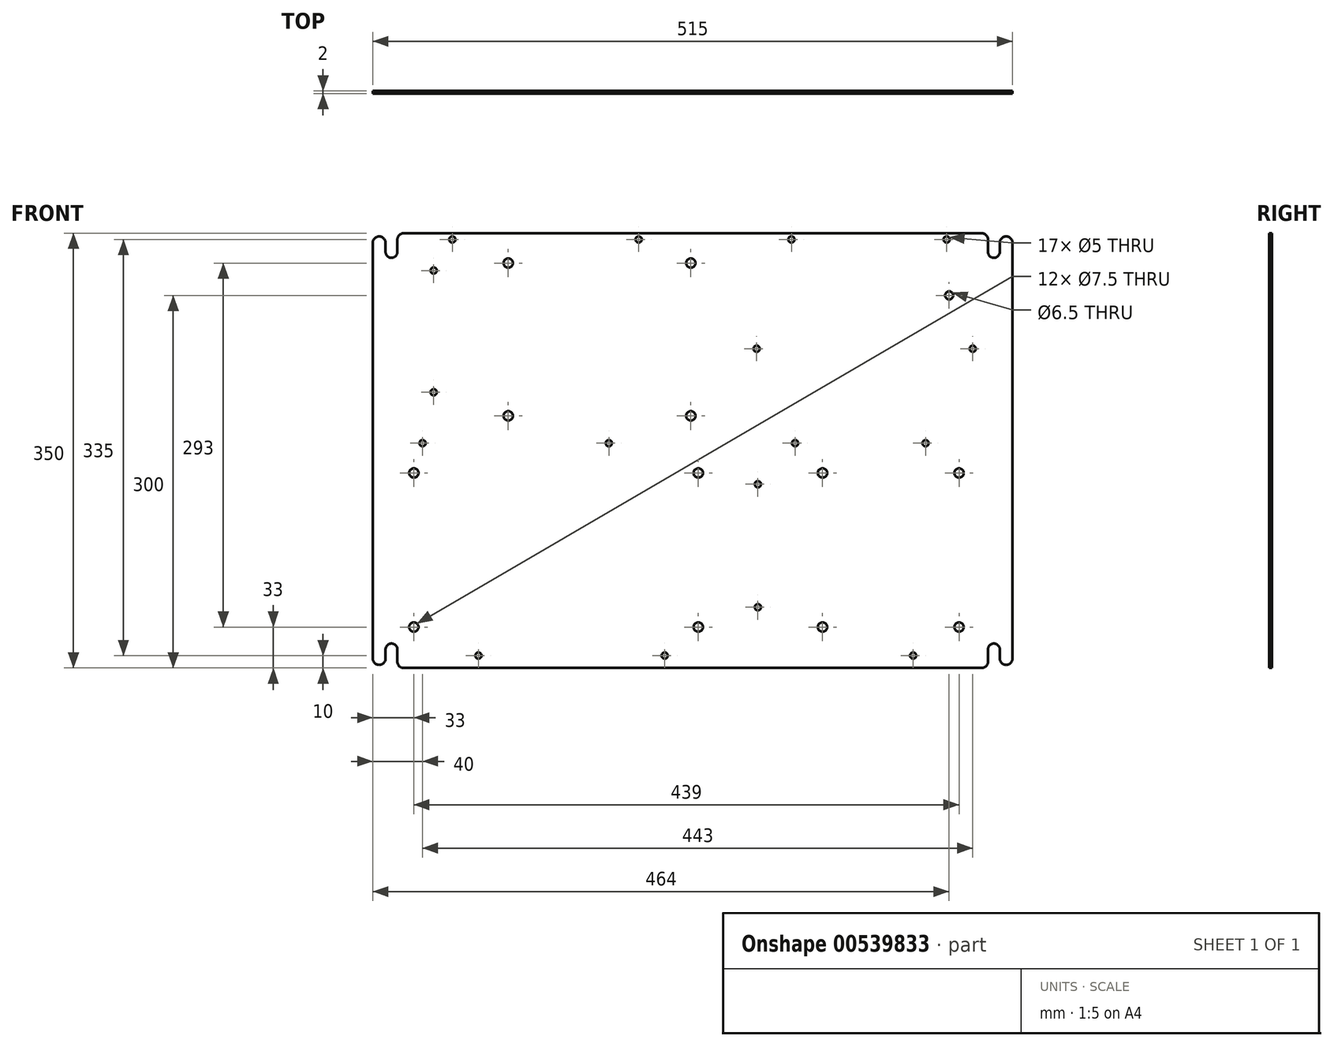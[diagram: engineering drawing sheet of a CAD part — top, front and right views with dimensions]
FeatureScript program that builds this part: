
annotation { "Feature Type Name" : "Feature", "Feature Type Description" : "" }
export const myFeature = defineFeature(function(context is Context, id is Id, definition is map)
    precondition{}
    {
        {
            var Q0;
            Q0=qCreatedBy(makeId("Front.planeOp"),FACE);
            var sketch = newSketch(context, id + "F0", { "sketchPlane" : qUnion([Q0])});
            skLineSegment(sketch, "E0.bottom", {"start": v(-257.5, -175) * mm, "end": v(232.75, -175) * mm});
            skLineSegment(sketch, "E0.top", {"start": v(-232.75, 175) * mm, "end": v(232.75, 175) * mm});
            skLineSegment(sketch, "E0.left", {"start": v(-257.5, -167.5) * mm, "end": v(-257.5, 167.5) * mm});
            skLineSegment(sketch, "E0.right", {"start": v(257.5, -167.5) * mm, "end": v(257.5, 167.5) * mm});
            skPoint(sketch, "E0.middle", {"position": v(0, 0) * mm});
            skArc(sketch, "E1", {"start": v(-247.25, 160) * mm, "mid": v(-242.5, 155.25) * mm, "end": v(-237.75, 160) * mm});
            skLineSegment(sketch, "E2", {"start": v(-247.25, 160) * mm, "end": v(-247.25, 167.5) * mm});
            skLineSegment(sketch, "E3", {"start": v(-237.75, 160) * mm, "end": v(-237.75, 170) * mm});
            skPoint(sketch, "E4.newPointB", {"position": v(-257.5, 175) * mm});
            skArc(sketch, "E4.filletArc", {"start": v(-232.75, 175) * mm, "mid": v(-236.29, 173.54) * mm, "end": v(-237.75, 170) * mm});
            skArc(sketch, "E5", {"start": v(-247.25, 167.5) * mm, "mid": v(-252.38, 172.48) * mm, "end": v(-257.5, 167.5) * mm});
            skPoint(sketch, "E5.endSnap0", {"position": v(-247.25, 167.5) * mm});
            skPoint(sketch, "E6.orphan", {"position": v(-247.25, 175) * mm});
            skArc(sketch, "E7.MirrorCS", {"start": v(247.25, 167.5) * mm, "mid": v(252.38, 172.48) * mm, "end": v(257.5, 167.5) * mm});
            skArc(sketch, "E8.MirrorCS", {"start": v(247.25, 160) * mm, "mid": v(242.5, 155.25) * mm, "end": v(237.75, 160) * mm});
            skLineSegment(sketch, "E9.MirrorCS", {"start": v(247.25, 160) * mm, "end": v(247.25, 167.5) * mm});
            skLineSegment(sketch, "E10.MirrorCS", {"start": v(237.75, 160) * mm, "end": v(237.75, 170) * mm});
            skArc(sketch, "E11.MirrorCS", {"start": v(232.75, 175) * mm, "mid": v(236.29, 173.54) * mm, "end": v(237.75, 170) * mm});
            skPoint(sketch, "E12.MirrorP", {"position": v(247.25, 175) * mm});
            skLineSegment(sketch, "E13.MirrorCS", {"start": v(232.75, 175) * mm, "end": v(-232.75, 175) * mm});
            skPoint(sketch, "E14.MirrorP", {"position": v(247.25, 167.5) * mm});
            skPoint(sketch, "E15.MirrorP", {"position": v(257.5, 175) * mm});
            skLineSegment(sketch, "E16.MirrorCS", {"start": v(232.75, -175) * mm, "end": v(-232.75, -175) * mm});
            skPoint(sketch, "E17.MirrorP", {"position": v(257.5, -175) * mm});
            skLineSegment(sketch, "E18.MirrorCS", {"start": v(257.5, 175) * mm, "end": v(257.5, -167.5) * mm});
            skLineSegment(sketch, "E19.MirrorCS", {"start": v(-232.75, -175) * mm, "end": v(232.75, -175) * mm});
            skLineSegment(sketch, "E20.MirrorCS", {"start": v(247.25, -160) * mm, "end": v(247.25, -167.5) * mm});
            skLineSegment(sketch, "E21.MirrorCS", {"start": v(237.75, -160) * mm, "end": v(237.75, -170) * mm});
            skArc(sketch, "E22.MirrorCS", {"start": v(247.25, -160) * mm, "mid": v(242.5, -155.25) * mm, "end": v(237.75, -160) * mm});
            skArc(sketch, "E23.MirrorCS", {"start": v(232.75, -175) * mm, "mid": v(236.29, -173.54) * mm, "end": v(237.75, -170) * mm});
            skPoint(sketch, "E24.MirrorP", {"position": v(247.25, -167.5) * mm});
            skPoint(sketch, "E25.MirrorP", {"position": v(247.25, -175) * mm});
            skArc(sketch, "E26.MirrorCS", {"start": v(247.25, -167.5) * mm, "mid": v(252.38, -172.48) * mm, "end": v(257.5, -167.5) * mm});
            skLineSegment(sketch, "E27.MirrorCS", {"start": v(-247.25, -160) * mm, "end": v(-247.25, -167.5) * mm});
            skArc(sketch, "E28.MirrorCS", {"start": v(-232.75, -175) * mm, "mid": v(-236.29, -173.54) * mm, "end": v(-237.75, -170) * mm});
            skArc(sketch, "E29.MirrorCS", {"start": v(-247.25, -167.5) * mm, "mid": v(-252.38, -172.48) * mm, "end": v(-257.5, -167.5) * mm});
            skArc(sketch, "E30.MirrorCS", {"start": v(-247.25, -160) * mm, "mid": v(-242.5, -155.25) * mm, "end": v(-237.75, -160) * mm});
            skLineSegment(sketch, "E31.MirrorCS", {"start": v(-237.75, -160) * mm, "end": v(-237.75, -170) * mm});
            skPoint(sketch, "E32.MirrorP", {"position": v(-247.25, -175) * mm});
            skLineSegment(sketch, "E33.MirrorCS", {"start": v(-257.5, 167.5) * mm, "end": v(-257.5, -167.5) * mm});
            skPoint(sketch, "E34.MirrorP", {"position": v(-247.25, -167.5) * mm});
            skPoint(sketch, "E35.MirrorP", {"position": v(-257.5, -175) * mm});
            skSolve(sketch);
        }
        {
            var Q0;
            Q0 = qSketchRegion(id + "F0", true);
            extrude(context, id + "F1", {"entities" : qUnion([Q0]), "depth" : 2 * mm, "offsetDistance" : 25 * mm});
        }
        {
            var Q0;
            Q0=makeQuery(id+"F1.opExtrude","CAP_FACE",FACE,{"disambiguationData":[OSD([sQuery(id+"F0.wireOp",EDGE,"E1"),sQuery(id+"F0.wireOp",EDGE,"E2"),sQuery(id+"F0.wireOp",EDGE,"E3"),sQuery(id+"F0.wireOp",EDGE,"E4.filletArc"),sQuery(id+"F0.wireOp",EDGE,"E5"),sQuery(id+"F0.wireOp",EDGE,"E7.MirrorCS"),sQuery(id+"F0.wireOp",EDGE,"E8.MirrorCS"),sQuery(id+"F0.wireOp",EDGE,"E9.MirrorCS"),sQuery(id+"F0.wireOp",EDGE,"E10.MirrorCS"),sQuery(id+"F0.wireOp",EDGE,"E11.MirrorCS"),sQuery(id+"F0.wireOp",EDGE,"E13.MirrorCS"),sQuery(id+"F0.wireOp",EDGE,"E20.MirrorCS"),sQuery(id+"F0.wireOp",EDGE,"E18.MirrorCS"),sQuery(id+"F0.wireOp",EDGE,"E21.MirrorCS"),sQuery(id+"F0.wireOp",EDGE,"E22.MirrorCS"),sQuery(id+"F0.wireOp",EDGE,"E23.MirrorCS"),sQuery(id+"F0.wireOp",EDGE,"E26.MirrorCS"),sQuery(id+"F0.wireOp",EDGE,"E27.MirrorCS"),sQuery(id+"F0.wireOp",EDGE,"E28.MirrorCS"),sQuery(id+"F0.wireOp",EDGE,"E29.MirrorCS"),sQuery(id+"F0.wireOp",EDGE,"E30.MirrorCS"),sQuery(id+"F0.wireOp",EDGE,"E31.MirrorCS"),sQuery(id+"F0.wireOp",EDGE,"E33.MirrorCS"),sQuery(id+"F0.wireOp",EDGE,"E19.MirrorCS")])],"isStart":false});
            var sketch = newSketch(context, id + "F2", { "sketchPlane" : qUnion([Q0])});
            skCircle(sketch, "E36", {"center": v(-172.5, -165) * mm, "radius": 2.5 * mm});
            skCircle(sketch, "E37", {"center": v(-22.5, -165) * mm, "radius": 2.5 * mm});
            skCircle(sketch, "E38", {"center": v(177.5, -165) * mm, "radius": 2.5 * mm});
            skCircle(sketch, "E39", {"center": v(-224.5, -142) * mm, "radius": 3.75 * mm});
            skCircle(sketch, "E40", {"center": v(-224.5, -18) * mm, "radius": 3.75 * mm});
            skCircle(sketch, "E41", {"center": v(4.5, -18) * mm, "radius": 3.75 * mm});
            skCircle(sketch, "E42", {"center": v(4.5, -142) * mm, "radius": 3.75 * mm});
            skCircle(sketch, "E43", {"center": v(52.5, -126) * mm, "radius": 2.5 * mm});
            skCircle(sketch, "E44", {"center": v(52.5, -27) * mm, "radius": 2.5 * mm});
            skCircle(sketch, "E45", {"center": v(104.5, -18) * mm, "radius": 3.75 * mm});
            skCircle(sketch, "E46", {"center": v(214.5, -18) * mm, "radius": 3.75 * mm});
            skCircle(sketch, "E47", {"center": v(104.5, -142) * mm, "radius": 3.75 * mm});
            skCircle(sketch, "E48", {"center": v(214.5, -142) * mm, "radius": 3.75 * mm});
            skCircle(sketch, "E49", {"center": v(-217.5, 6) * mm, "radius": 2.5 * mm});
            skCircle(sketch, "E50", {"center": v(-67.5, 6) * mm, "radius": 2.5 * mm});
            skCircle(sketch, "E51", {"center": v(82.5, 6) * mm, "radius": 2.5 * mm});
            skCircle(sketch, "E52", {"center": v(187.5, 6) * mm, "radius": 2.5 * mm});
            skCircle(sketch, "E53", {"center": v(-193.5, 170) * mm, "radius": 2.5 * mm});
            skCircle(sketch, "E54", {"center": v(-208.5, 47) * mm, "radius": 2.5 * mm});
            skCircle(sketch, "E55", {"center": v(-208.5, 145) * mm, "radius": 2.5 * mm});
            skCircle(sketch, "E56", {"center": v(-148.5, 28) * mm, "radius": 3.75 * mm});
            skCircle(sketch, "E57", {"center": v(-148.5, 151) * mm, "radius": 3.75 * mm});
            skCircle(sketch, "E58", {"center": v(-1.5, 151) * mm, "radius": 3.75 * mm});
            skCircle(sketch, "E59", {"center": v(-1.5, 28) * mm, "radius": 3.75 * mm});
            skCircle(sketch, "E60", {"center": v(51.5, 82) * mm, "radius": 2.5 * mm});
            skCircle(sketch, "E61", {"center": v(225.5, 82) * mm, "radius": 2.5 * mm});
            skCircle(sketch, "E62", {"center": v(206.5, 125) * mm, "radius": 3.25 * mm});
            skCircle(sketch, "E63", {"center": v(-43.5, 170) * mm, "radius": 2.5 * mm});
            skCircle(sketch, "E64", {"center": v(79.5, 170) * mm, "radius": 2.5 * mm});
            skCircle(sketch, "E65", {"center": v(204.5, 170) * mm, "radius": 2.5 * mm});
            skSolve(sketch);
        }
        {
            var Q0;
            Q0 = qSketchRegion(id + "F2", true);
            extrude(context, id + "F3", {"entities" : qUnion([Q0]), "operationType" : NewBodyOperationType.REMOVE, "oppositeDirection" : true, "depth" : 25 * mm, "offsetDistance" : 25 * mm});
        }
    });
